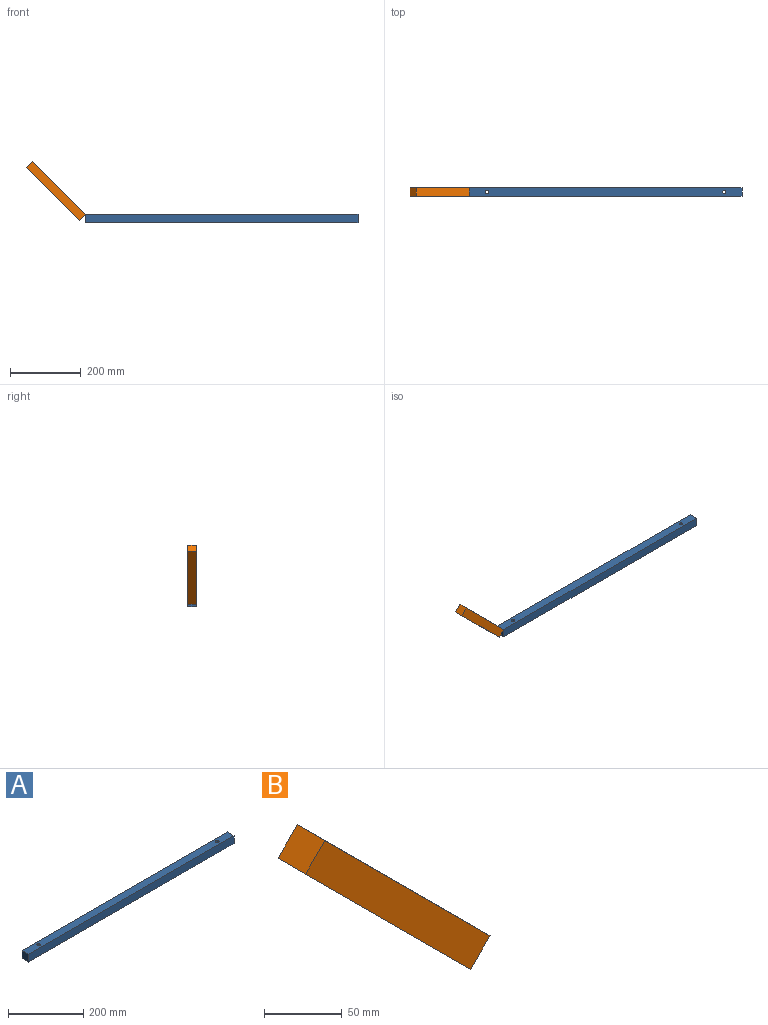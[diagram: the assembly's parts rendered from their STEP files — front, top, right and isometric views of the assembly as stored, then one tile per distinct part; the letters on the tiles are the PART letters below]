
ASSEMBLY  parts=2 mates=1
PART A: 8 faces, bbox 770x25x25 mm
  f0: plane 770x25mm, normal (0,-1,0), area 19250mm2, adj f1,f3,f4,f5
  f1: plane 25x25mm, normal (1,0,0), area 625mm2, adj f0,f2,f4,f5
  f2: plane 770x25mm, normal (0,1,0), area 19250mm2, adj f1,f3,f4,f5
  f3: plane 25x25mm, normal (-1,0,0), area 625mm2, adj f0,f2,f4,f5
  f4: plane 770x25mm, normal (0,0,1), area 19122.8mm2, adj f0,f1,f2,f3,f6,f7
  f5: plane 770x25mm, normal (0,0,-1), area 19122.8mm2, adj f0,f1,f2,f3,f6,f7
  f6: cylinder r=4.5mm len=25mm, axis (0,0,-1), area 706.9mm2, adj f4,f5
  f7: cylinder r=4.5mm len=25mm, axis (0,0,-1), area 706.9mm2, adj f4,f5
PART B: 6 faces, bbox 167.7x25x167.7 mm
  f0: plane 25x17.68mm, normal (-0.71,0,0.71), area 625mm2, adj f1,f3,f4,f5
  f1: plane 150x150mm, normal (-0.71,0,-0.71), area 5303.3mm2, adj f0,f2,f4,f5
  f2: plane 25x17.68mm, normal (0.71,0,-0.71), area 625mm2, adj f1,f3,f4,f5
  f3: plane 150x150mm, normal (0.71,0,0.71), area 5303.3mm2, adj f0,f2,f4,f5
  f4: plane 167.68x167.68mm, normal (0,-1,0), area 5303.3mm2, adj f0,f1,f2,f3
  f5: plane 167.68x167.68mm, normal (0,1,0), area 5303.3mm2, adj f0,f1,f2,f3
PLACE A t=(402.68,-25,81.68)mm
PLACE B t=(0,0,89)mm
MATE fastened A.f0 <-> B.f4  axis (0,-1,0) through (17.68,-25,106.68)mm
